# Revit family: ElectricalFixture_WiringAccessories_Hager_Sollysta_FlatSwitchDimmers
name_source: partatom
category: Lighting Fixtures
revit_build: Autodesk Revit 2015 (Build: 20160512_1515(x64)
units: mm (PartAtom-declared; Revit-internal decimal feet)

## types (16) — shared parameters
CE Approval = Yes
Default Elevation = 1219.2 mm  [stored 4 ft]
Design Country = China
Expected Life = 25 years
Extrusion From Wall = 3 mm  [stored 0.00984252 ft]
Frequency = 50/60Hz
Gross Weight kg = 0.165
LED Indicator Switch = No
Manufacturer = Hager
Manufacturer Country = United Kingdom
Manufacturer Website = http://www.hager.co.uk
Overall Height = 86 mm  [stored 0.282152 ft]
Packaging Recyclable = Yes
Product Family = DecorativeDimmers_SwitchDimmers
Product Group = WiringAccessories
Product Literature = http://www.hager.co.uk
Product Range = Sollysta
Product URL = http://www.hager.co.uk
Reference Standard = BS 1363-2
Shape = Rectangular
Shipping Weight kg = 0.188
Supply Phase = 1
Switch = No
Type = ElectricalFixture
Voltage (Volts) = 230V/240V
zero-valued in all types: Overall Width

## per-type parameters (varying)
| type | 1 Gang | 2 Gang | 3 Gang | 4 Gang | Colour | Description | EAN Code | Features | Finish | Material | Name | Overall Depth | Overall Length | Product Model Number | Technical Description | Unique Reference |
| WFDS1PS | Yes | No | No | No | PolishedSteel | 1GangDimmerSwitch400WPolishedSteel | 5015654793005 | 1GangDimmerSwitch400WPolishedSteel | Polished | Hager_PolishedSteel | DecorativeDimmers_WFDS1PS | 28.5 mm | 86 mm  [stored 0.282152 ft] | WFDS1PS | 1GangDimmerSwitch400WPolishedSteel | WFDS1PS |
| WFDS2PS | No | Yes | No | No | PolishedSteel | 2GangDimmerSwitch250WPolishedSteel | 5015654793029 | 2GangDimmerSwitch250WPolishedSteel | Polished | Hager_PolishedSteel | DecorativeDimmers_WFDS2PS | 26.1 mm | 86 mm  [stored 0.282152 ft] | WFDS2PS | 2GangDimmerSwitch250WPolishedSteel | WFDS2PS |
| WFDS1BS | Yes | No | No | No | BrushedSteel | 1GangDimmerSwitch400WBrushedSteel | 5015654792992 | 1GangDimmerSwitch400WBrushedSteel | Brushed | Hager_BrushedSteel | DecorativeDimmers_WFDS1BS | 28.5 mm | 86 mm  [stored 0.282152 ft] | WFDS1BS | 1GangDimmerSwitch400WBrushedSteel | WFDS1BS |
| WFDS1PB | Yes | No | No | No | PolishedBrass | 1GangDimmerSwitch400WPolishedBrass | 5015654740955 | 1GangDimmerSwitch400WPolishedBrass | Polished | Hager_PolishedBrass | DecorativeDimmers_WFDS1PB | 28.5 mm | 86 mm  [stored 0.282152 ft] | WFDS1PB | 1GangDimmerSwitch400WPolishedBrass | WFDS1PB |
| WFDS1BN | Yes | No | No | No | BlackNickel | 1GangDimmerSwitch400WBlackNickel | 5015654740986 | 1GangDimmerSwitch400WBlackNickel | Polished | Hager_BlackNickel | DecorativeDimmers_WFDS1BN | 28.5 mm | 86 mm  [stored 0.282152 ft] | WFDS1BN | 1GangDimmerSwitch400WBlackNickel | WFDS1PS |
| WFDS3BS | Yes | No | Yes | No | BrushedSteel | 3GangDimmerSwitch250WBrushedSteel | 5015654793036 | 3GangDimmerSwitch250WBrushedSteel | Brushed | Hager_BrushedSteel | DecorativeDimmers_WFDS3BS | 28.5 mm | 146 mm  [stored 0.479003 ft] | WFDS3BS | 3GangDimmerSwitch250WBrushedSteel | WFDS3BS |
| WFDS2PB | No | Yes | No | No | PolishedBrass | 2GangDimmerSwitch250WPolishedBrass | 5015654741037 | 2GangDimmerSwitch250WPolishedBrass | Polished | Hager_PolishedBrass | DecorativeDimmers_WFDS2PB | 28.5 mm | 86 mm  [stored 0.282152 ft] | WFDS1PB | 2GangDimmerSwitch250WPolishedBrass | WFDS2PB |
| WFDS2BN | No | Yes | No | No | BlackNickel | 2GangDimmerSwitch250WBlackNickel | 5015654741051 | 2GangDimmerSwitch250WBlackNickel | Polished | Hager_BlackNickel | DecorativeDimmers_WFDS2BN | 28.5 mm | 86 mm  [stored 0.282152 ft] | WFDS2BN | 2GangDimmerSwitch250WBlackNickel | WFDS1PS |
| WFDS3PS | Yes | No | Yes | No | PolishedSteel | 3GangDimmerSwitch250WPolishedSteel | 5015654793043 | 3GangDimmerSwitch250WPolishedSteel | Polished | Hager_PolishedSteel | DecorativeDimmers_WFD32PS | 26.1 mm | 146 mm  [stored 0.479003 ft] | WFDS3PS | 3GangDimmerSwitch250WPolishedSteel | WFDS2PS |
| WFDS2BS | No | Yes | No | No | BrushedSteel | 2GangDimmerSwitch250WBrushedSteel | 5015654793036 | 2GangDimmerSwitch250WBrushedSteel | Brushed | Hager_BrushedSteel | DecorativeDimmers_WFDS2BS | 28.5 mm | 86 mm  [stored 0.282152 ft] | WFDS2BS | 2GangDimmerSwitch250WBrushedSteel | WFDS3BS |
| WFDS3PB | Yes | No | Yes | No | PolishedBrass | 3GangDimmerSwitch250WPolishedBrass | 5015654741112 | 3GangDimmerSwitch250WPolishedBrass | Polished | Hager_PolishedBrass | DecorativeDimmers_WFDS3PB | 28.5 mm | 146 mm  [stored 0.479003 ft] | WFDS3PB | 3GangDimmerSwitch250WPolishedBrass | WFDS3PB |
| WFDS3BN | Yes | No | Yes | No | BlackNickel | 3GangDimmerSwitch250WBlackNickel | 5015654741136 | 3GangDimmerSwitch250WBlackNickel | Polished | Hager_BlackNickel | DecorativeDimmers_WFDS3BN | 28.5 mm | 146 mm  [stored 0.479003 ft] | WFDS3BN | 3GangDimmerSwitch250WBlackNickel | WFDS3PS |
| WFDS4BN | No | Yes | No | Yes | BlackNickel | 4GangDimmerSwitch250WBlackNickel | 5015654741211 | 4GangDimmerSwitch250WBlackNickel | Polished | Hager_BlackNickel | DecorativeDimmers_WFDS4BN | 28.5 mm | 146 mm  [stored 0.479003 ft] | WFDS4BN | 4GangDimmerSwitch250WBlackNickel | WFDS3PS |
| WFDS4PS | No | Yes | No | Yes | PolishedSteel | 4GangDimmerSwitch250WPolishedSteel | 5015654793067 | 4GangDimmerSwitch250WPolishedSteel | Polished | Hager_PolishedSteel | DecorativeDimmers_WFDS4PS | 26.1 mm | 146 mm  [stored 0.479003 ft] | WFDS4PS | 4GangDimmerSwitch250WPolishedSteel | WFDS4PS |
| WFDS4PB | No | Yes | No | Yes | PolishedBrass | 4GangDimmerSwitch250WPolishedBrass | 5015654741198 | 4GangDimmerSwitch250WPolishedBrass | Polished | Hager_PolishedBrass | DecorativeDimmers_WFDS4PB | 28.5 mm | 146 mm  [stored 0.479003 ft] | WFDS4PB | 4GangDimmerSwitch250WPolishedBrass | WFDS3PB |
| WFDS4BS | No | Yes | No | Yes | BrushedSteel | 4GangDimmerSwitch250WBrushedSteel | 5015654793050 | 4GangDimmerSwitch250WBrushedSteel | Brushed | Hager_BrushedSteel | DecorativeDimmers_WFD43BS | 28.5 mm | 146 mm  [stored 0.479003 ft] | WFDS4BS | 4GangDimmerSwitch250WBrushedSteel | WFDS4BS |

note: [stored X ft] marks values corroborated as IEEE doubles in the binary element streams (Revit-internal decimal feet)

## geometry (parser evidence)
native form markers: Blend x4, Sweep x2
no freeform markers — native parametric forms only
